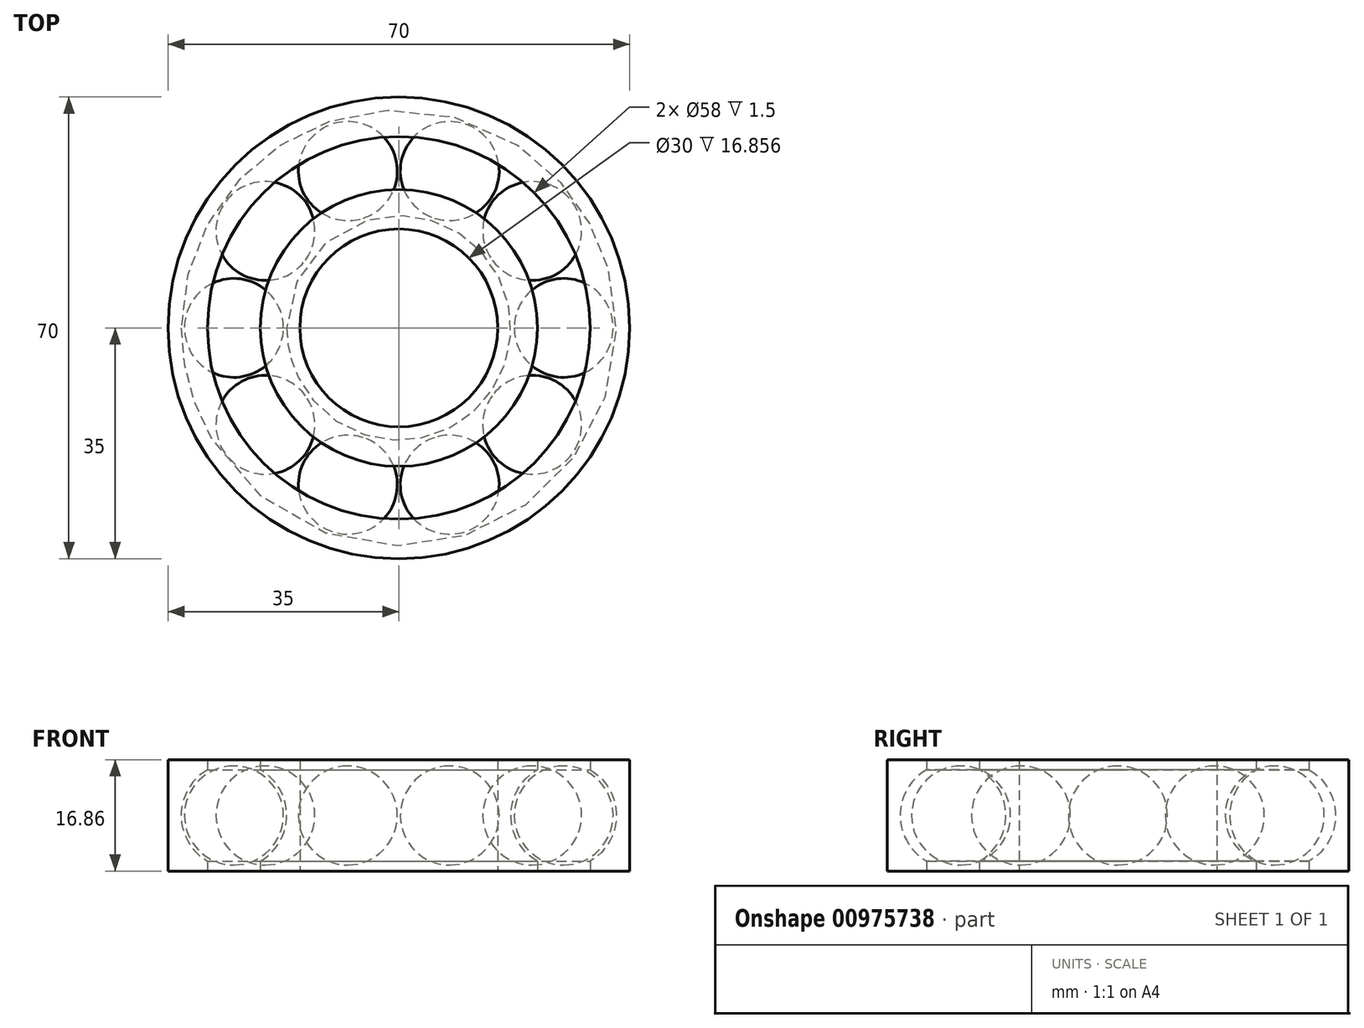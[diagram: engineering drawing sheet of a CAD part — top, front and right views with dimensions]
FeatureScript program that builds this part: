
annotation { "Feature Type Name" : "Feature", "Feature Type Description" : "" }
export const myFeature = defineFeature(function(context is Context, id is Id, definition is map)
    precondition{}
    {
        {
            var Q0;
            Q0=qCreatedBy(makeId("Front.planeOp"),FACE);
            var sketch = newSketch(context, id + "F0", { "sketchPlane" : qUnion([Q0])});
            skCircle(sketch, "E0", {"center": v(25, 0) * mm, "radius": 7.5 * mm});
            skCircle(sketch, "E1", {"center": v(25, 0) * mm, "radius": 8 * mm});
            skLineSegment(sketch, "E2", {"start": v(21, -6.93) * mm, "end": v(21, -8.43) * mm});
            skLineSegment(sketch, "E3", {"start": v(21, -8.43) * mm, "end": v(0, -8.43) * mm});
            skLineSegment(sketch, "E4", {"start": v(0, -8.43) * mm, "end": v(0, 8.43) * mm, "construction": true});
            skLineSegment(sketch, "E5", {"start": v(0, 8.43) * mm, "end": v(21, 8.43) * mm});
            skLineSegment(sketch, "E6", {"start": v(21, 8.43) * mm, "end": v(21, 6.93) * mm});
            skLineSegment(sketch, "E7", {"start": v(29, 6.93) * mm, "end": v(29, 8.43) * mm});
            skLineSegment(sketch, "E8", {"start": v(29, 8.43) * mm, "end": v(35, 8.43) * mm});
            skLineSegment(sketch, "E9", {"start": v(35, 8.43) * mm, "end": v(35, -8.43) * mm});
            skLineSegment(sketch, "E10", {"start": v(35, -8.43) * mm, "end": v(29, -8.43) * mm});
            skLineSegment(sketch, "E11", {"start": v(29, -8.43) * mm, "end": v(29, -6.93) * mm});
            skLineSegment(sketch, "E12", {"start": v(15, 8.43) * mm, "end": v(15, -8.43) * mm});
            skLineSegment(sketch, "E13", {"start": v(25, -7.5) * mm, "end": v(25, 7.5) * mm});
            skSolve(sketch);
        }
        {
            var Q0;
            {var subQ0=sQuery(id+"F0.wireOp",EDGE,"E13");Q0=makeQuery(id+"F0.imprint","IMPRINT",FACE,{"disambiguationData":[TD([[makeQuery(id+"F0.imprint","IMPRINT",EDGE,{"derivedFrom":subQ0}),-1.0]])]});}
            var Q1;
            Q1=sQuery(id+"F0.wireOp",EDGE,"E13");
            revolve(context, id + "F1", {"surfaceOperationType" : NewSurfaceOperationType.NEW, "entities" : qUnion([Q0]), "axis" : qUnion([Q1]), "revolveType" : RevolveType.FULL});
        }
        {
            var Q0;
            {var subQ1=sQuery(id+"F0.wireOp",EDGE,"E2");Q0=makeQuery(id+"F0.imprint","IMPRINT",FACE,{"disambiguationData":[TD([[makeQuery(id+"F0.imprint","IMPRINT",EDGE,{"derivedFrom":subQ1}),-1.0]])]});}
            var Q1;
            {var subQ0=sQuery(id+"F0.wireOp",EDGE,"E7");Q1=makeQuery(id+"F0.imprint","IMPRINT",FACE,{"disambiguationData":[TD([[makeQuery(id+"F0.imprint","IMPRINT",EDGE,{"derivedFrom":subQ0}),-1.0]])]});}
            var Q2;
            Q2=sQuery(id+"F0.wireOp",EDGE,"E4");
            revolve(context, id + "F2", {"surfaceOperationType" : NewSurfaceOperationType.NEW, "entities" : qUnion([Q0, Q1]), "axis" : qUnion([Q2]), "revolveType" : RevolveType.FULL});
        }
        {
            var Q0;
            Q0=makeQuery(id+"F1.opRevolve","SWEPT_BODY",BODY,{"disambiguationData":[OSD([sQuery(id+"F0.wireOp",EDGE,"E0"),sQuery(id+"F0.wireOp",EDGE,"E13")])]});
            var Q1;
            Q1=makeQuery(id+"F2.opRevolve","SWEPT_EDGE",EDGE,{"disambiguationData":[OSD([sQuery(id+"F0.wireOp",EDGE,"E5"),sQuery(id+"F0.wireOp",EDGE,"E12")])]});
            circularPattern(context, id + "F3", {"entities" : qUnion([Q0]), "axis" : qUnion([Q1]), "angle" : 360 * degree, "instanceCount" : 10, "equalSpace" : true});
        }
    });
